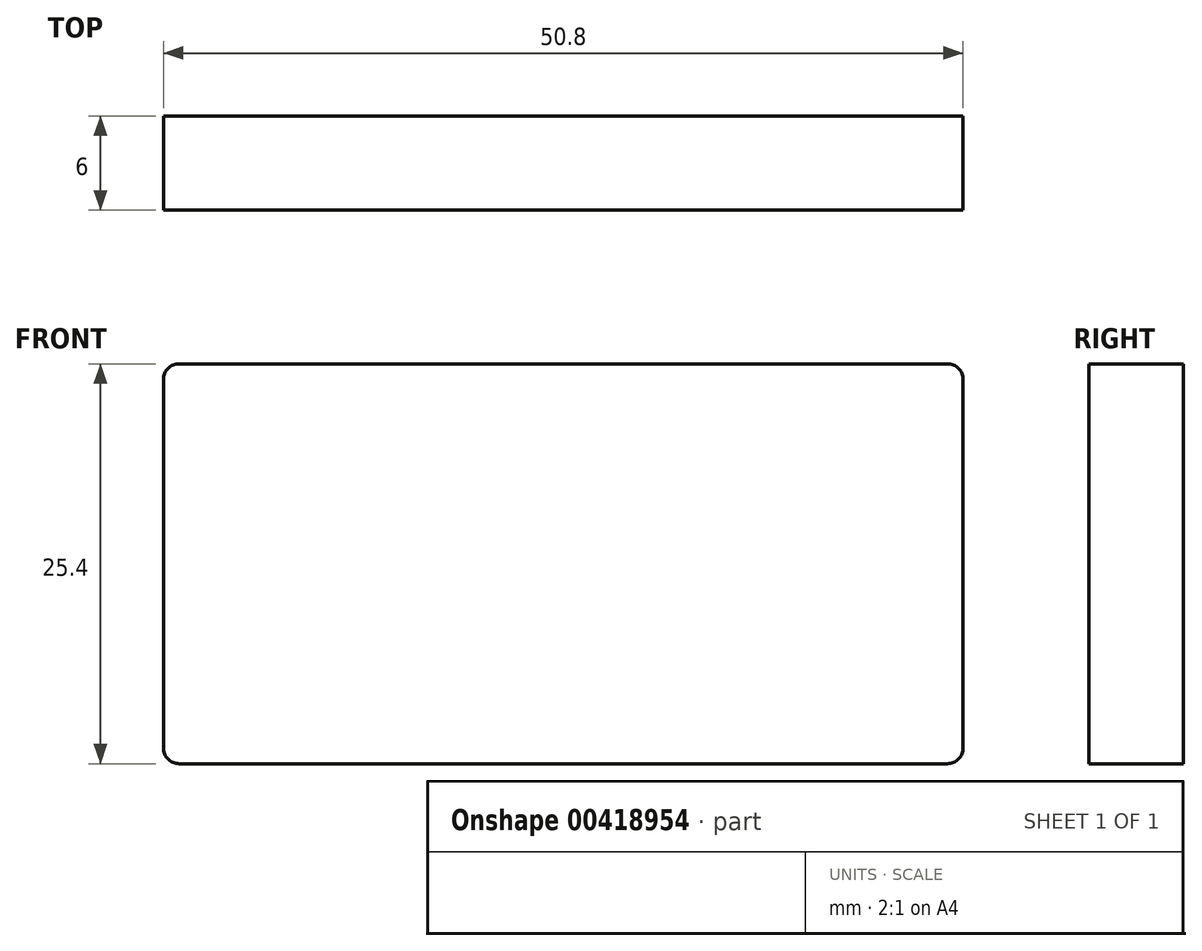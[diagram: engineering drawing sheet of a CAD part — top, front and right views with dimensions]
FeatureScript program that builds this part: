
annotation { "Feature Type Name" : "Feature", "Feature Type Description" : "" }
export const myFeature = defineFeature(function(context is Context, id is Id, definition is map)
    precondition{}
    {
        {
            var Q0;
            Q0=qCreatedBy(makeId("Front.planeOp"),FACE);
            var sketch = newSketch(context, id + "F0", { "sketchPlane" : qUnion([Q0])});
            skLineSegment(sketch, "E0.bottom", {"start": v(0, 0) * mm, "end": v(-50.8, 0) * mm});
            skLineSegment(sketch, "E0.top", {"start": v(0, 25.4) * mm, "end": v(-50.8, 25.4) * mm});
            skLineSegment(sketch, "E0.left", {"start": v(0, 0) * mm, "end": v(0, 25.4) * mm});
            skLineSegment(sketch, "E0.right", {"start": v(-50.8, 0) * mm, "end": v(-50.8, 25.4) * mm});
            skSolve(sketch);
        }
        {
            var Q0;
            Q0 = qSketchRegion(id + "F0", true);
            extrude(context, id + "F1", {"entities" : qUnion([Q0]), "depth" : 6 * mm});
        }
        {
            var Q0;
            Q0=makeQuery(id+"F1.opExtrude","SWEPT_EDGE",EDGE,{"disambiguationData":[OSD([sQuery(id+"F0.wireOp",EDGE,"E0.top"),sQuery(id+"F0.wireOp",EDGE,"E0.right")])]});
            var Q1;
            Q1=makeQuery(id+"F1.opExtrude","SWEPT_EDGE",EDGE,{"disambiguationData":[OSD([sQuery(id+"F0.wireOp",EDGE,"E0.bottom"),sQuery(id+"F0.wireOp",EDGE,"E0.right")])]});
            var Q2;
            Q2=makeQuery(id+"F1.opExtrude","SWEPT_EDGE",EDGE,{"disambiguationData":[OSD([sQuery(id+"F0.wireOp",EDGE,"E0.bottom"),sQuery(id+"F0.wireOp",EDGE,"E0.left")])]});
            var Q3;
            Q3=makeQuery(id+"F1.opExtrude","SWEPT_EDGE",EDGE,{"disambiguationData":[OSD([sQuery(id+"F0.wireOp",EDGE,"E0.top"),sQuery(id+"F0.wireOp",EDGE,"E0.left")])]});
            fillet(context, id + "F2", {"entities" : qUnion([Q0, Q1, Q2, Q3]), "radius" : 1 * mm, "tangentPropagation" : true, "allowEdgeOverflow" : false});
        }
    });
